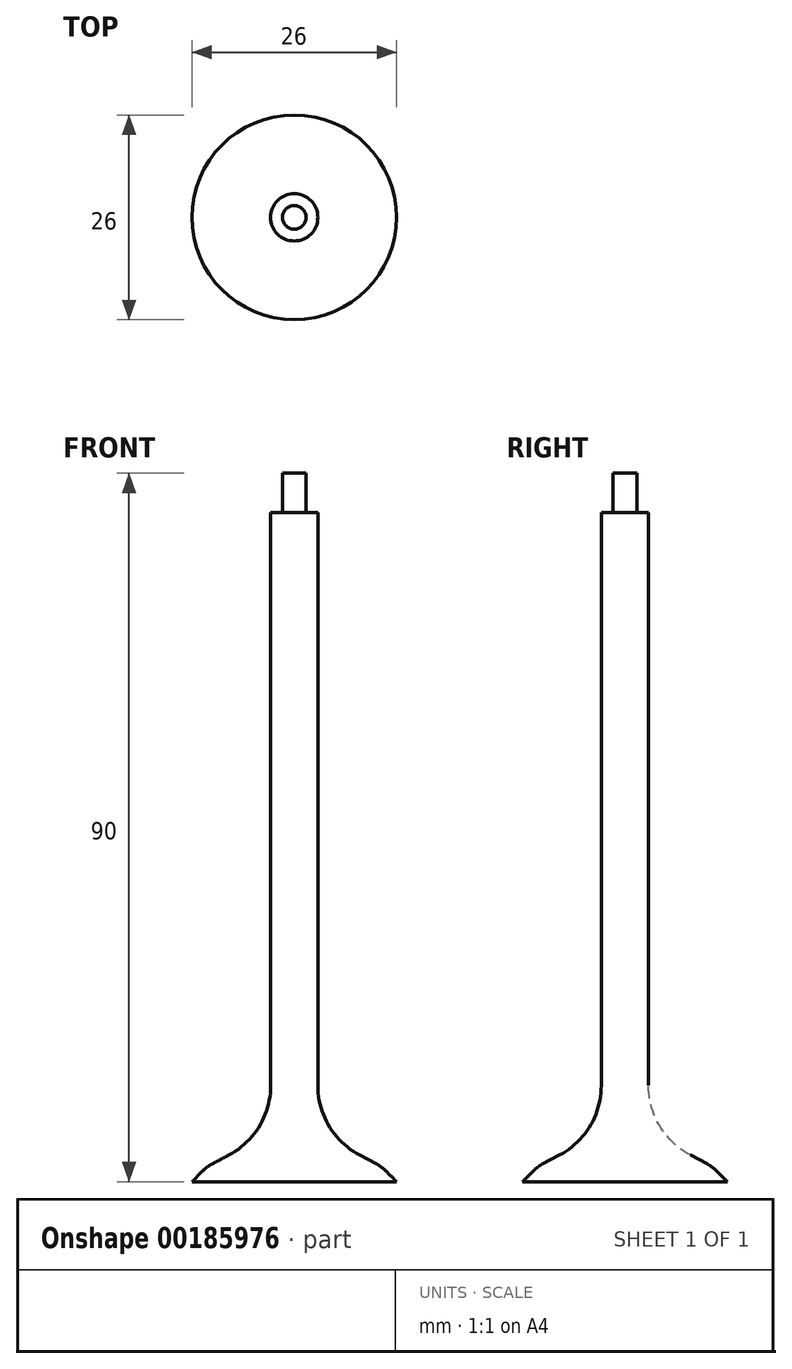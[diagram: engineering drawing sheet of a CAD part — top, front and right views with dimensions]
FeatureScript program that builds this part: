
annotation { "Feature Type Name" : "Feature", "Feature Type Description" : "" }
export const myFeature = defineFeature(function(context is Context, id is Id, definition is map)
    precondition{}
    {
        {
            var Q0;
            Q0=qCreatedBy(makeId("Front.planeOp"),FACE);
            var sketch = newSketch(context, id + "F0", { "sketchPlane" : qUnion([Q0])});
            skLineSegment(sketch, "E0", {"start": v(0, 0) * mm, "end": v(13, 0) * mm});
            skLineSegment(sketch, "E1", {"start": v(13, 0) * mm, "end": v(11.11, 1.89) * mm});
            skLineSegment(sketch, "E2", {"start": v(11.11, 1.89) * mm, "end": v(3, 6.2) * mm});
            skLineSegment(sketch, "E3", {"start": v(3, 6.2) * mm, "end": v(3, 85) * mm});
            skLineSegment(sketch, "E4", {"start": v(3, 85) * mm, "end": v(1.5, 85) * mm});
            skLineSegment(sketch, "E5", {"start": v(1.5, 85) * mm, "end": v(1.5, 90) * mm});
            skLineSegment(sketch, "E6", {"start": v(1.5, 90) * mm, "end": v(0, 90) * mm});
            skLineSegment(sketch, "E7", {"start": v(0, 90) * mm, "end": v(0, 0) * mm});
            skSolve(sketch);
        }
        {
            var Q0;
            Q0 = qSketchRegion(id + "F0", true);
            var Q1;
            Q1=sQuery(id+"F0.wireOp",EDGE,"E7");
            revolve(context, id + "F1", {"entities" : qUnion([Q0]), "axis" : qUnion([Q1]), "revolveType" : RevolveType.FULL});
        }
        {
            var Q0;
            Q0=makeQuery(id+"F1.opRevolve","SWEPT_EDGE",EDGE,{"disambiguationData":[OSD([sQuery(id+"F0.wireOp",EDGE,"E2"),sQuery(id+"F0.wireOp",EDGE,"E3")])]});
            fillet(context, id + "F2", {"entities" : qUnion([Q0]), "radius" : 10 * mm, "tangentPropagation" : true, "allowEdgeOverflow" : false});
        }
        {
            var Q0;
            Q0=makeQuery(id+"F1.opRevolve","SWEPT_EDGE",EDGE,{"disambiguationData":[OSD([sQuery(id+"F0.wireOp",EDGE,"E1"),sQuery(id+"F0.wireOp",EDGE,"E2")])]});
            fillet(context, id + "F3", {"entities" : qUnion([Q0]), "radius" : 5 * mm, "tangentPropagation" : true, "allowEdgeOverflow" : false});
        }
    });
